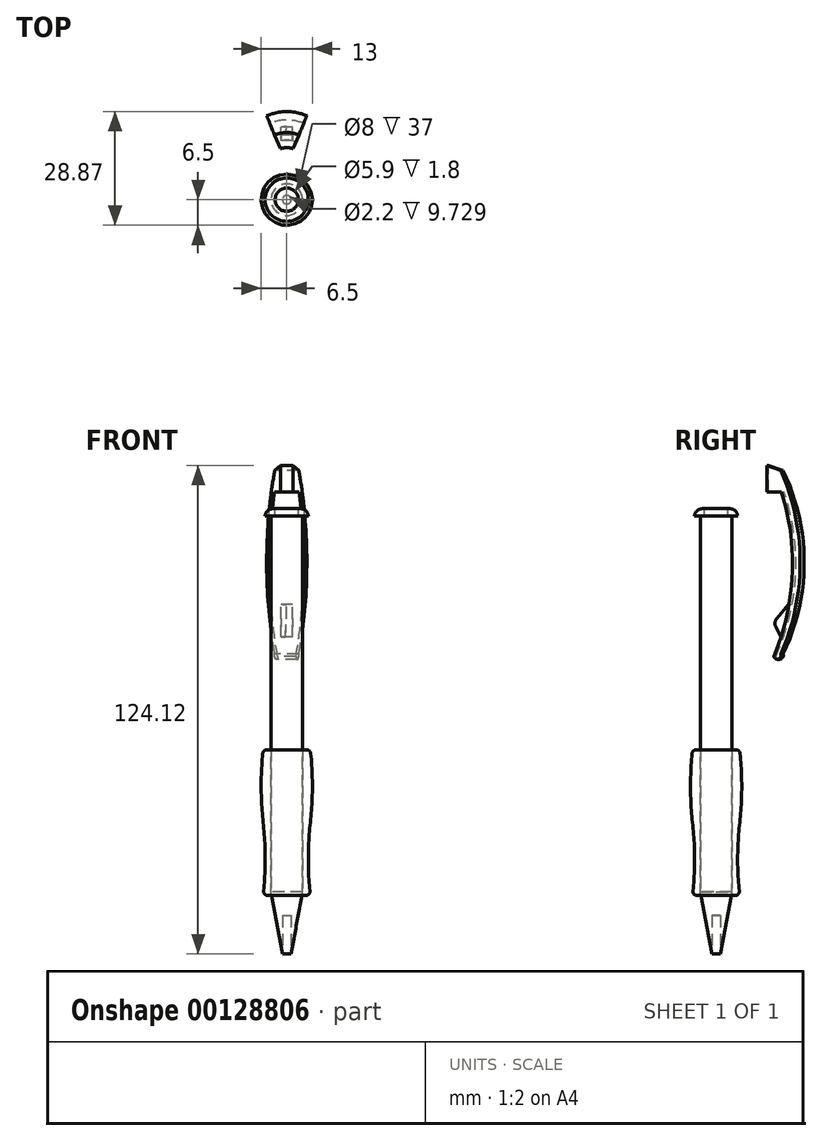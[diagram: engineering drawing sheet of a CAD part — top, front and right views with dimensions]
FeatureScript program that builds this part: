
annotation { "Feature Type Name" : "Feature", "Feature Type Description" : "" }
export const myFeature = defineFeature(function(context is Context, id is Id, definition is map)
    precondition{}
    {
        {
            var Q0;
            Q0=qCreatedBy(makeId("Top.planeOp"),FACE);
            var sketch = newSketch(context, id + "F0", { "sketchPlane" : qUnion([Q0])});
            skCircle(sketch, "E0", {"center": v(0, 0) * mm, "radius": 4 * mm});
            skSolve(sketch);
        }
        {
            var Q0;
            Q0 = qSketchRegion(id + "F0", true);
            extrude(context, id + "F1", {"entities" : qUnion([Q0]), "endBound" : BoundingType.SYMMETRIC, "depth" : 95.58 * mm});
        }
        {
            var Q0;
            Q0=makeQuery(id+"F1.opExtrude","CAP_FACE",FACE,{"disambiguationData":[OSD([sQuery(id+"F0.wireOp",EDGE,"E0")])],"isStart":true});
            cPlane(context, id + "F2", {"entities" : qUnion([Q0]), "cplaneType" : CPlaneType.OFFSET, "offset" : 16 * mm, "width" : 150 * mm, "height" : 150 * mm});
        }
        {
            var Q0;
            Q0=qCreatedBy(makeId("Right.planeOp"),FACE);
            var sketch = newSketch(context, id + "F3", { "sketchPlane" : qUnion([Q0])});
            skLineSegment(sketch, "E1", {"start": v(46.35, -6.28) * mm, "end": v(46.35, -6.28) * mm});
            skLineSegment(sketch, "E2", {"start": v(13.25, 60.6) * mm, "end": v(13.25, 53.86) * mm});
            skLineSegment(sketch, "E3", {"start": v(13.25, 53.86) * mm, "end": v(17.25, 53.86) * mm});
            skLineSegment(sketch, "E4", {"start": v(13.25, 60.6) * mm, "end": v(17.02, 59.29) * mm});
            skArc(sketch, "E5", {"start": v(15.14, 12.01) * mm, "mid": v(20.17, 32.74) * mm, "end": v(17.25, 53.86) * mm});
            skArc(sketch, "E6", {"start": v(17.02, 12.68) * mm, "mid": v(22.37, 35.98) * mm, "end": v(17.02, 59.29) * mm});
            skArc(sketch, "E7", {"start": v(15.14, 12.01) * mm, "mid": v(16.42, 11.4) * mm, "end": v(17.02, 12.68) * mm});
            skLineSegment(sketch, "E8", {"start": v(9.04, 65) * mm, "end": v(9.04, 29.55) * mm});
            skSolve(sketch);
        }
        {
            var Q0;
            Q0 = qSketchRegion(id + "F3", true);
            var Q1;
            Q1=sQuery(id+"F3.wireOp",EDGE,"E8");
            revolve(context, id + "F4", {"entities" : qUnion([Q0]), "axis" : qUnion([Q1]), "revolveType" : RevolveType.SYMMETRIC, "angle" : 45 * degree});
        }
        {
            var Q0;
            Q0=qCreatedBy(makeId("Front.planeOp"),FACE);
            var sketch = newSketch(context, id + "F5", { "sketchPlane" : qUnion([Q0])});
            skLineSegment(sketch, "E9", {"start": v(-4, -48.66) * mm, "end": v(-4, -11.66) * mm});
            skLineSegment(sketch, "E10", {"start": v(-4, -11.66) * mm, "end": v(-5.1, -11.66) * mm});
            skLineSegment(sketch, "E11", {"start": v(-4, -48.66) * mm, "end": v(-4.89, -48.66) * mm});
            skPoint(sketch, "E12", {"position": v(-6, -30.16) * mm});
            skArc(sketch, "E13", {"start": v(-6.1, -12.56) * mm, "mid": v(-6.5, -21.37) * mm, "end": v(-6, -30.16) * mm});
            skArc(sketch, "E14", {"start": v(-5.88, -47.56) * mm, "mid": v(-5.47, -38.86) * mm, "end": v(-6, -30.16) * mm});
            skPoint(sketch, "E15.visualSharp", {"position": v(-6, -11.66) * mm});
            skArc(sketch, "E15.filletArc", {"start": v(-5.1, -11.66) * mm, "mid": v(-5.77, -11.92) * mm, "end": v(-6.1, -12.56) * mm});
            skPoint(sketch, "E16.visualSharp", {"position": v(-6, -48.66) * mm});
            skArc(sketch, "E16.filletArc", {"start": v(-5.88, -47.56) * mm, "mid": v(-5.63, -48.33) * mm, "end": v(-4.89, -48.66) * mm});
            skSolve(sketch);
        }
        {
            assignVariable(context, id + "F6", {"name" : "top", "anyValue" : 1.8});
        }
        {
            var Q0;
            Q0=makeQuery(id+"F1.opExtrude","CAP_FACE",FACE,{"disambiguationData":[OSD([sQuery(id+"F0.wireOp",EDGE,"E0")])],"isStart":false});
            var sketch = newSketch(context, id + "F7", { "sketchPlane" : qUnion([Q0])});
            skCircle(sketch, "E17", {"center": v(0, 0) * mm, "radius": 5.5 * mm});
            skSolve(sketch);
        }
        {
            var Q0;
            Q0 = qSketchRegion(id + "F7", true);
            extrude(context, id + "F8", {"entities" : qUnion([Q0]), "depth" : (getVariable(context, 'top')) * mm});
        }
        {
            var Q0;
            Q0=makeQuery(id+"F8.opExtrude","CAP_FACE",FACE,{"disambiguationData":[OSD([sQuery(id+"F7.wireOp",EDGE,"E17")])],"isStart":false});
            var sketch = newSketch(context, id + "F9", { "sketchPlane" : qUnion([Q0])});
            skCircle(sketch, "E18", {"center": v(0, 0) * mm, "radius": 2.95 * mm});
            skSolve(sketch);
        }
        {
            var Q0;
            Q0 = qSketchRegion(id + "F9", true);
            extrude(context, id + "F10", {"entities" : qUnion([Q0]), "operationType" : NewBodyOperationType.REMOVE, "oppositeDirection" : true, "depth" : (getVariable(context, 'top')) * mm});
        }
        {
            var Q0;
            Q0=makeQuery(id+"F8.opExtrude","CAP_EDGE",EDGE,{"disambiguationData":[OSD([sQuery(id+"F7.wireOp",EDGE,"E17")])],"isStart":false});
            fillet(context, id + "F11", {"entities" : qUnion([Q0]), "radius" : 2 * mm, "tangentPropagation" : true, "allowEdgeOverflow" : false});
        }
        {
            var Q0;
            Q0=qCreatedBy(id+"F2.planeOp",FACE);
            var sketch = newSketch(context, id + "F12", { "sketchPlane" : qUnion([Q0])});
            skCircle(sketch, "E19", {"center": v(0, 0) * mm, "radius": 1.1 * mm});
            skCircle(sketch, "E20", {"center": v(0, 0) * mm, "radius": 1.05 * mm});
            skSolve(sketch);
        }
        {
            var Q1;
            Q1=makeQuery(id+"F1.opExtrude","CAP_FACE",FACE,{"disambiguationData":[OSD([sQuery(id+"F0.wireOp",EDGE,"E0")])],"isStart":true});
            var Q2;
            Q2=makeQuery(id+"F12.imprint","IMPRINT",FACE,{"disambiguationData":[TD([[makeQuery(id+"F12.imprint","IMPRINT",EDGE,{"derivedFrom":sQuery(id+"F12.wireOp",EDGE,"E20")}),1.0]])]});
            loft(context, id + "F13", {"operationType" : NewBodyOperationType.ADD, "sheetProfilesArray" : [{ "sheetProfileEntities" : qUnion([Q1]) }, { "sheetProfileEntities" : qUnion([Q2]) }]});
        }
        {
            var Q0;
            Q0=makeQuery(id+"F12.imprint","IMPRINT",FACE,{"disambiguationData":[TD([[makeQuery(id+"F12.imprint","IMPRINT",EDGE,{"derivedFrom":sQuery(id+"F12.wireOp",EDGE,"E20")}),1.0]])]});
            var Q1;
            Q1=makeQuery(id+"F12.imprint","IMPRINT",FACE,{"disambiguationData":[TD([[makeQuery(id+"F12.imprint","IMPRINT",EDGE,{"derivedFrom":sQuery(id+"F12.wireOp",EDGE,"E19")}),1.0]])]});
            extrude(context, id + "F14", {"entities" : qUnion([Q0, Q1]), "operationType" : NewBodyOperationType.REMOVE, "oppositeDirection" : true, "depth" : 10 * mm});
        }
        {
            var Q0;
            Q0=qCreatedBy(makeId("Right.planeOp"),FACE);
            var sketch = newSketch(context, id + "F15", { "sketchPlane" : qUnion([Q0])});
            skArc(sketch, "E21", {"start": v(16.45, 17.02) * mm, "mid": v(17.76, 21.08) * mm, "end": v(18.42, 25.29) * mm});
            skLineSegment(sketch, "E22", {"start": v(15.43, 21.68) * mm, "end": v(18.42, 25.29) * mm});
            skLineSegment(sketch, "E23", {"start": v(16.45, 17.02) * mm, "end": v(15.19, 19.5) * mm});
            skPoint(sketch, "E24.visualSharp", {"position": v(14.59, 20.67) * mm});
            skArc(sketch, "E24.filletArc", {"start": v(15.43, 21.68) * mm, "mid": v(14.98, 20.62) * mm, "end": v(15.19, 19.5) * mm});
            skSolve(sketch);
        }
        {
            var Q0;
            Q0 = qSketchRegion(id + "F15", true);
            extrude(context, id + "F16", {"entities" : qUnion([Q0]), "operationType" : NewBodyOperationType.ADD, "endBound" : BoundingType.SYMMETRIC, "depth" : 3 * mm});
        }
        {
            var Q0;
            Q0=makeQuery(id+"F16.opExtrude","CAP_FACE",FACE,{"disambiguationData":[OSD([sQuery(id+"F15.wireOp",EDGE,"E21"),sQuery(id+"F15.wireOp",EDGE,"E22"),sQuery(id+"F15.wireOp",EDGE,"E23"),sQuery(id+"F15.wireOp",EDGE,"E24.filletArc")])],"isStart":true});
            var Q1;
            Q1=sQuery(id+"F3.wireOp",EDGE,"E8");
            revolve(context, id + "F17", {"operationType" : NewBodyOperationType.ADD, "entities" : qUnion([Q0]), "axis" : qUnion([Q1]), "revolveType" : RevolveType.ONE_DIRECTION, "angle" : 9 * degree});
        }
        {
            var Q0;
            Q0=qCreatedBy(makeId("Front.planeOp"),FACE);
            var sketch = newSketch(context, id + "F18", { "sketchPlane" : qUnion([Q0])});
            skLineSegment(sketch, "E25", {"start": v(0, 0) * mm, "end": v(0, -69.83) * mm});
            skSolve(sketch);
        }
        {
            var Q0;
            Q0 = qSketchRegion(id + "F5", true);
            var Q1;
            Q1=sQuery(id+"F18.wireOp",EDGE,"E25");
            revolve(context, id + "F19", {"entities" : qUnion([Q0]), "axis" : qUnion([Q1]), "revolveType" : RevolveType.FULL});
        }
    });
